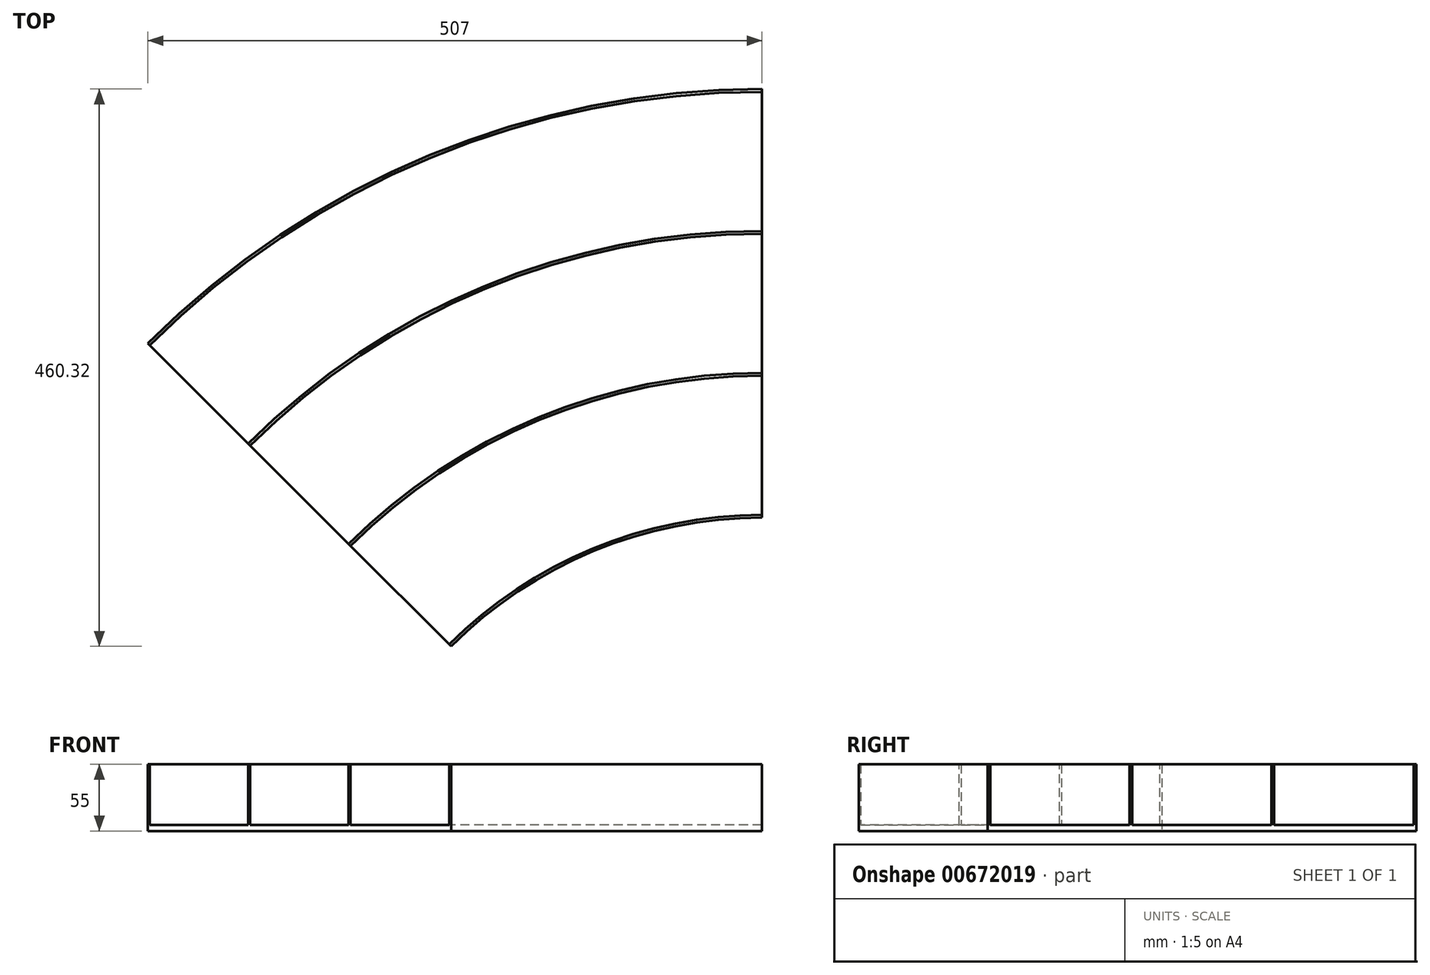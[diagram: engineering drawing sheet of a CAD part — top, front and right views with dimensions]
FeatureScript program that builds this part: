
annotation { "Feature Type Name" : "Feature", "Feature Type Description" : "" }
export const myFeature = defineFeature(function(context is Context, id is Id, definition is map)
    precondition{}
    {
        {
            var Q0;
            Q0=qCreatedBy(makeId("Top.planeOp"),FACE);
            var sketch = newSketch(context, id + "F0", { "sketchPlane" : qUnion([Q0])});
            skLineSegment(sketch, "E0", {"start": v(0, 363) * mm, "end": v(0, 717) * mm});
            skArc(sketch, "E1", {"start": v(0, 717) * mm, "mid": v(-274.38, 662.42) * mm, "end": v(-507, 507) * mm});
            skArc(sketch, "E2", {"start": v(0, 363) * mm, "mid": v(-138.91, 335.37) * mm, "end": v(-256.68, 256.68) * mm});
            skArc(sketch, "E3", {"start": v(0, 540) * mm, "mid": v(-206.65, 498.9) * mm, "end": v(-381.84, 381.84) * mm, "construction": true});
            skArc(sketch, "E4", {"start": v(0, 714.75) * mm, "mid": v(-273.52, 660.34) * mm, "end": v(-505.4, 505.4) * mm});
            skArc(sketch, "E5", {"start": v(0, 599.75) * mm, "mid": v(-229.51, 554.1) * mm, "end": v(-424.09, 424.09) * mm});
            skArc(sketch, "E6", {"start": v(0, 597.5) * mm, "mid": v(-228.65, 552.02) * mm, "end": v(-422.5, 422.5) * mm});
            skArc(sketch, "E7", {"start": v(0, 482.5) * mm, "mid": v(-184.64, 445.77) * mm, "end": v(-341.18, 341.18) * mm});
            skArc(sketch, "E8", {"start": v(0, 480.25) * mm, "mid": v(-183.78, 443.7) * mm, "end": v(-339.59, 339.59) * mm});
            skArc(sketch, "E9", {"start": v(0, 365.25) * mm, "mid": v(-139.78, 337.45) * mm, "end": v(-258.27, 258.27) * mm});
            skLineSegment(sketch, "E10", {"start": v(-256.68, 256.68) * mm, "end": v(-507, 507) * mm});
            skSolve(sketch);
        }
        {
            var Q0;
            Q0=qCreatedBy(makeId("Right.planeOp"),FACE);
            var sketch = newSketch(context, id + "F1", { "sketchPlane" : qUnion([Q0])});
            skLineSegment(sketch, "E11", {"start": v(363, -5) * mm, "end": v(363, 50) * mm});
            skLineSegment(sketch, "E12", {"start": v(363, 50) * mm, "end": v(365.25, 50) * mm});
            skLineSegment(sketch, "E13", {"start": v(365.25, 50) * mm, "end": v(365.25, 0) * mm});
            skLineSegment(sketch, "E14", {"start": v(365.25, 0) * mm, "end": v(480.25, 0) * mm});
            skLineSegment(sketch, "E15", {"start": v(480.25, 0) * mm, "end": v(480.25, 50) * mm});
            skLineSegment(sketch, "E16", {"start": v(480.25, 50) * mm, "end": v(482.5, 50) * mm});
            skLineSegment(sketch, "E17", {"start": v(482.5, 50) * mm, "end": v(482.5, 0) * mm});
            skLineSegment(sketch, "E18", {"start": v(482.5, 0) * mm, "end": v(597.5, 0) * mm});
            skLineSegment(sketch, "E19", {"start": v(597.5, 0) * mm, "end": v(597.5, 50) * mm});
            skLineSegment(sketch, "E20", {"start": v(597.5, 50) * mm, "end": v(599.75, 50) * mm});
            skLineSegment(sketch, "E21", {"start": v(599.75, 50) * mm, "end": v(599.75, 0) * mm});
            skLineSegment(sketch, "E22", {"start": v(599.75, 0) * mm, "end": v(714.75, 0) * mm});
            skLineSegment(sketch, "E23", {"start": v(714.75, 0) * mm, "end": v(714.75, 50) * mm});
            skLineSegment(sketch, "E24", {"start": v(714.75, 50) * mm, "end": v(717, 50) * mm});
            skLineSegment(sketch, "E25", {"start": v(717, 50) * mm, "end": v(717, -5) * mm});
            skLineSegment(sketch, "E26", {"start": v(717, -5) * mm, "end": v(363, -5) * mm});
            skSolve(sketch);
        }
        {
            var Q0;
            Q0 = qSketchRegion(id + "F1", true);
            var Q1;
            Q1=sQuery(id+"F0.wireOp",EDGE,"E2");
            sweep(context, id + "F2", {"profiles" : qUnion([Q0]), "path" : qUnion([Q1])});
        }
    });
